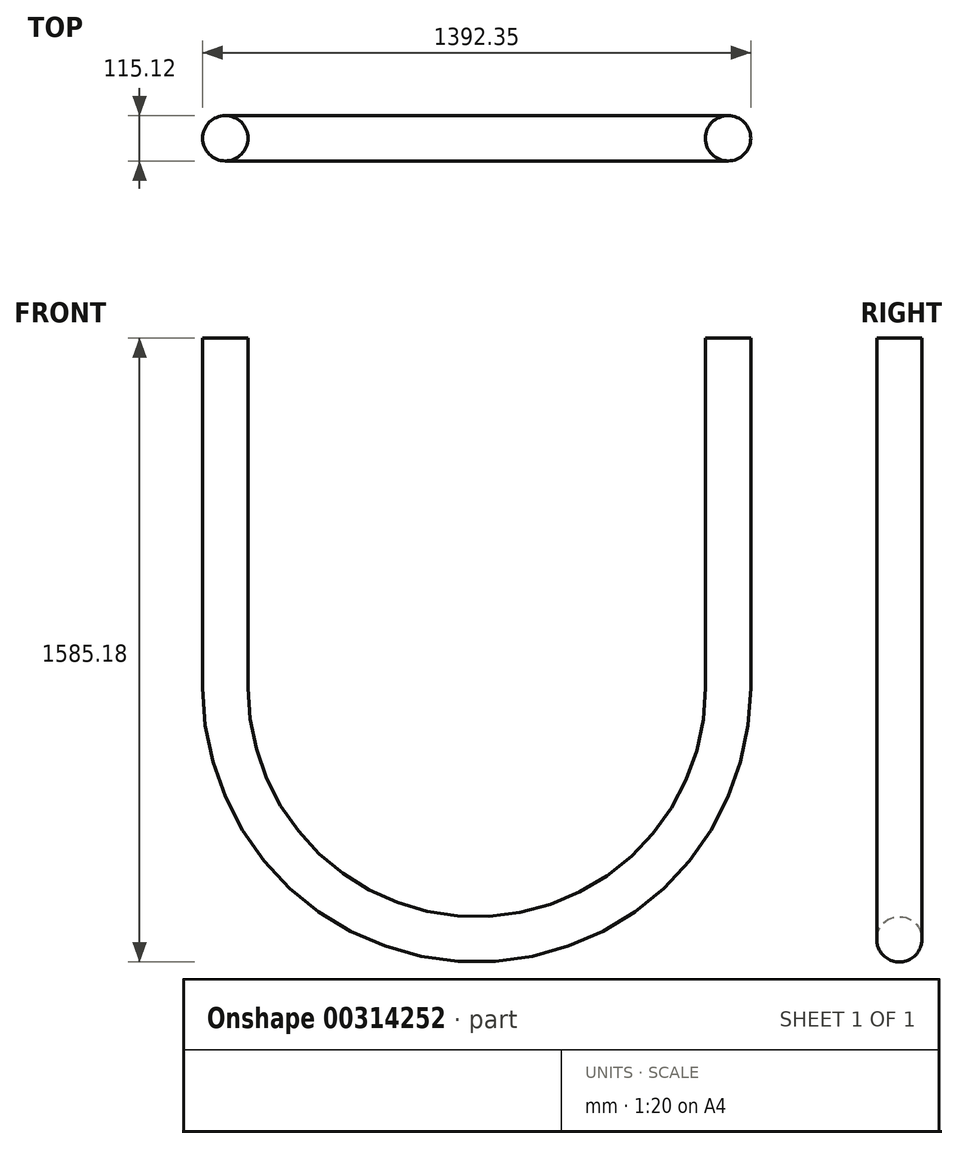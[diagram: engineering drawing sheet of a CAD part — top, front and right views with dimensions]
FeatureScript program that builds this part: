
annotation { "Feature Type Name" : "Feature", "Feature Type Description" : "" }
export const myFeature = defineFeature(function(context is Context, id is Id, definition is map)
    precondition{}
    {
        {
            var Q0;
            Q0=qCreatedBy(makeId("Front.planeOp"),FACE);
            var sketch = newSketch(context, id + "F0", { "sketchPlane" : qUnion([Q0])});
            skLineSegment(sketch, "E0", {"start": v(-570.6, 0) * mm, "end": v(-570.6, -889) * mm});
            skLineSegment(sketch, "E1", {"start": v(699.4, -889) * mm, "end": v(699.4, 0) * mm});
            skArc(sketch, "E2", {"start": v(-570.6, -889) * mm, "mid": v(64.4, -1524) * mm, "end": v(699.4, -889) * mm});
            skSolve(sketch);
        }
        {
            var Q0;
            Q0=qCreatedBy(makeId("Top.planeOp"),FACE);
            var sketch = newSketch(context, id + "F1", { "sketchPlane" : qUnion([Q0])});
            skCircle(sketch, "E3", {"center": v(703.03, 0) * mm, "radius": 57.56 * mm});
            skSolve(sketch);
        }
        {
            var Q0;
            Q0=makeQuery(id+"F1.imprint","IMPRINT",FACE,{"disambiguationData":[TD([[makeQuery(id+"F1.imprint","IMPRINT",EDGE,{"derivedFrom":sQuery(id+"F1.wireOp",EDGE,"E3")}),1.0]])]});
            var Q1;
            Q1=sQuery(id+"F0.wireOp",EDGE,"E1");
            var Q2;
            Q2=sQuery(id+"F0.wireOp",EDGE,"E2");
            var Q3;
            Q3=sQuery(id+"F0.wireOp",EDGE,"E0");
            sweep(context, id + "F2", {"profiles" : qUnion([Q0]), "path" : qUnion([Q1, Q2, Q3])});
        }
    });
